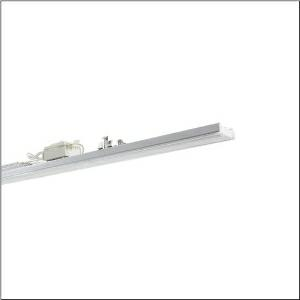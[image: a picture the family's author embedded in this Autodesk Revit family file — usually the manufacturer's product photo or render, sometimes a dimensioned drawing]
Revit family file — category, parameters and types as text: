
# Revit family: licross_r__11_recessed_ho_51tl18mv4hxm_c411
name_source: partatom
category: Lighting Fixtures
units: mm (PartAtom-declared; Revit-internal decimal feet)

## family parameters
Cut with Voids When Loaded = No
Host = Face
Light Source = No
Part Type = Normal
Room Calculation Point = No
Round Connector Dimension = Use Diameter
Shared = No

## types (1)
- --- (1 x LED, 17090 lm, 89.2 W, 4000K)
    Apparent Load = 89 VA
    CIE Flux Codes = 78 94 99 100 100
    Color Rendering = 80
    Color Temperature = 4000K
    Default Elevation = 1800 mm
    Description = Licross® 11 Recessed HO, luminaire insert, of sheet steel, coil coated, white, length: 2.250mm, width: 66mm, height: 67mm, LED rated luminous flux: 17.090lm, light colour: 840, control gear: ON/OFF Multilumen, with plug, 3-pole, with phase selection, mains connection: 220..240V, AC, 50/60Hz, rated input power: 89W, halogen-free wiring, primary light control with lens, of plastic, primary optical cover: cover, of PMMA, light emission: direct distribution, primary light characteristic: symmetric, protection rating (complete): IP40, insulation class (complete): insulation class I (protective earthing), certification: CE, ENEC, VDE, UKCA, protection symbol: D if used in an environment without relevant dust loads with corresponding accessories, impact resistance: IK06, permissible ambient temperature for indoor applications: -35..+35°C, corresponds to IFS (International Featured Standards) requirements for safety and quality in the food industry, reducing of maximum allowable ambient temperature of 5°C with ceiling mounting, packaging unit: 1 piece
    Height = 58 mm
    Lamp = 1 x LED
    Lamp Light Flux = 17090 lm
    Lamp Power = 89.2 W
    Lamp count = 1
    Length = 2250 mm
    Luminous efficacy = 192 lm/W
    Manufacturer = Siteco
    ModVariant = No
    Model = 51TL18MV4HXM
    Mounting Place = Ceiling
    Mounting Type = Pendant
    Number of Poles = 1
    OnlyDefault = Yes
    Power Factor = 1
    Product Name = Licross® 11 Recessed HO
    Product group = luminaire insert
    ProductGroupID = 902
    Protection Class = Protection class I
    Protection Degree = IP 40
    RLX_Detail_Level = 1
    RLX_Emergency_Light_Flux = 0 lm
    RLX_Emergency_Type = 0
    RLX_Emergency_Type_DB = No
    RlxData = <blob elided: 27085 chars, md5=5e1244fe>
    Socket = socket
    Standby Power = 0 W
    System Light Flux = 17090 lm
    System Power = 89 W
    Type Comments = factory setting: luminous flux: 100 % | (A | C | E) | 210 mA
    Type Image = l_1296930.jpg
    URL = http://relux.com
    VarID = @adj_084698
    Voltage = 0 V
    Weight = 0.00 kg
    Width = 66 mm

## geometry (parser evidence)
native form markers: Blend x4, Sweep x9
no freeform markers — native parametric forms only
